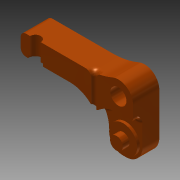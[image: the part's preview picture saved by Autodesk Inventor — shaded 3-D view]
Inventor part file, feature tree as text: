
AUTODESK INVENTOR PART (.ipt)
format: ipt  version: 2013 (Build 170138000, 138)  size: 234,496 bytes
history: native  units: in
note: dims shown in document units (in); Inventor stores cm internally (conversion verified against a paired STEP export)
features: extrude x8, sketch x8, reference x5, fillet x4
ambient origin geometry x8: Origin, YZ Plane, XZ Plane, XY Plane, X Axis, Y Axis, Z Axis, Center Point
bodies: Solid1 (feature_tree)
feature tree (25):
  extrude  "Extrusion1"  Depth=0.4331in
  extrude  "Extrusion2"  Depth=0.2953in
  extrude  "Extrusion3"  Depth=0.8268in
  extrude  "Extrusion4"  Depth=0.3858in TaperAngle=0.0deg
  fillet  "Fillet1"  Radius=0.7874in
  fillet  "Fillet2"  Radius=0.189in
  extrude  "Extrusion5"  Depth=0.4134in
  extrude  "Extrusion6"  Depth=0.0787in
  fillet  "Fillet3"  Radius=0.0787in
  extrude  "Extrusion7"  Depth=0.0394in TaperAngle=0.0deg
  fillet  "Fillet4"  Radius=0.2205in
  extrude  "Extrusion8"  Depth=0.0787in
  sketch  "Sketch1"  dims[d0=0.189in d3=0.4331in]
  reference  "Reference1"
  reference  "Reference2"
  reference  "Reference3"
  sketch  "Sketch2"  dims[d5=0.8287in d6=0.2953in]
  reference  "Reference4"
  sketch  "Sketch3"  dims[d7=0.9843in d8=0.8268in]
  sketch  "Sketch4"  dims[d9=0.3858in d10=0.0in d11=0.3858in d12=0.0in d13=0.7874in d16=0.189in]
  sketch  "Sketch5"  dims[d17=0.0984in d18=0.0in d19=0.4134in]
  sketch  "Sketch6"  dims[d23=0.0394in d24=0.0in d25=0.0787in d26=0.0787in]
  sketch  "Sketch7"  dims[d27=0.1575in d29=0.0394in d30=0.0in d31=0.2205in]
  reference  "Reference5"
  sketch  "Sketch8"  dims[d34=0.0394in d35=0.0in d36=0.0787in d37=0.0984in d38=0.0in d39=0.0787in d40=0.0787in d43=0.0039in d44=0.1181in d46=1.0in d47=0.0in]
